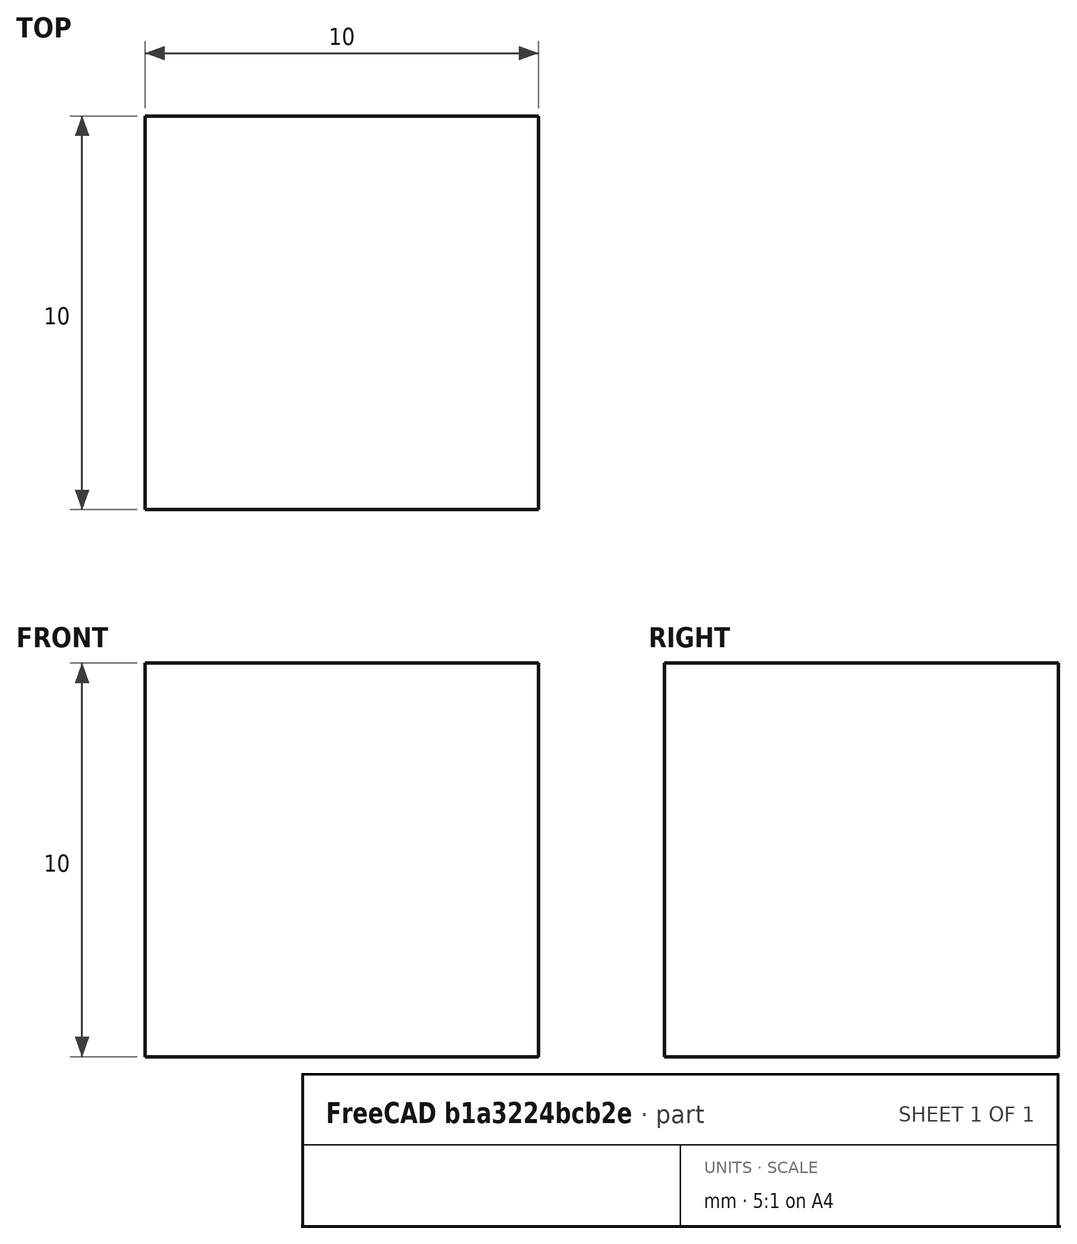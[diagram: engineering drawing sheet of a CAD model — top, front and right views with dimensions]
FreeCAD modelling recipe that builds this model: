
FCSTD DOCUMENT  (FreeCAD 0.21R33694 (Git))
Label: VM_Uniaxial_Tension_Example
License: All rights reserved
LicenseURL: http://en.wikipedia.org/wiki/All_rights_reserved
objects: Fem::ConstraintPressure×3, Fem::FemMeshObjectPython×2, Fem::ConstraintDisplacement×2, Part::Box×1, Fem::FemSolverObjectPython×1, App::MaterialObjectPython×1, Fem::ConstraintFixed×1, Fem::FemPostPipeline×1, Fem::FemResultObjectPython×1, Fem::FemAnalysis×1
note: 1 computed .brp shape members not serialized (recipe doc carries the construction recipe); baked Part::Feature solids carry a one-line shape summary decoded from their .brp

FEATURE [Part::Box] Box  label="Cube"
  AttacherType = Attacher::AttachEngine3D
  Height = 10
  Length = 10
  Width = 10
FEATURE [Fem::FemSolverObjectPython] SolverCcxTools  # FEM object (typed FeaturePython)
  AnalysisType = 0
  BeamShellResultOutput3D = false
  BucklingFactors = 1
  EigenmodeHighLimit = 1000000
  EigenmodeLowLimit = 0
  EigenmodesCount = 10
  GeometricalNonlinearity = 0
  IterationsControlParameterCutb = 0.25,0.5,0.75,0.85,,,1.5,
  IterationsControlParameterIter = 4,8,9,200,10,400,,200,,
  IterationsControlParameterTimeUse = false
  IterationsThermoMechMaximum = 2000
  IterationsUserDefinedIncrementations = false
  IterationsUserDefinedTimeStepLength = false
  MaterialNonlinearity = 0
  MatrixSolverType = 0
  SplitInputWriter = false
  ThermoMechSteadyState = true
  TimeEnd = 1
  TimeInitialStep = 0.01
FEATURE [Fem::FemMeshObjectPython] FEMMeshGmsh  # FEM object (typed FeaturePython)
  Algorithm2D = 0
  Algorithm3D = 0
  CharacteristicLengthMax = 10
  CharacteristicLengthMin = 10
  CoherenceMesh = true
  ElementDimension = 0
  ElementOrder = 1
  GeometryTolerance = 1e-06
  GroupsOfNodes = false
  HighOrderOptimize = 0
  MeshSizeFromCurvature = 12
  OptimizeNetgen = false
  OptimizeStd = true
  Part = -> Box
  RecombinationAlgorithm = 0
  Recombine3DAll = false
  RecombineAll = false
  SecondOrderLinear = false
FEATURE [Fem::ConstraintPressure] ConstraintPressure
  NormalDirection = (1,0,0)
  Normals = (18) [(1,0,0),(1,0,0),(1,0,0),(1,0,0),(1,0,0),(1,0,0),(1,0,0),(1,0,0),(1,0,0),(-1,0,0),(-1,0,0),(-1,0,0),(-1,0,0),(-1,0,0),(-1,0,0),(-1,0,0),(-1,0,0),+1 more]
  Points = (18) [(10,10,0),(10,10,5),(10,10,10),(10,5,0),(10,5,5),(10,5,10),(10,0,0),(10,0,5),(10,0,10),(0,10,0),(0,10,5),(0,10,10),(0,5,0),(0,5,5),(0,5,10),(0,0,0),+2 more]
  Pressure = 10
  References = -> [Box]
  Reversed = true
FEATURE [App::MaterialObjectPython] MaterialSolid  # material (typed FeaturePython)
  Category = 0
  Material = AuthorAndLicense=(c) 2013 Yorik van Havre (CC-BY 3.0),CardName=Concrete-Generic,CompressiveStrength=25 MPa,Density=2400 kg/m^3,+7 more (map truncated)
  References = -> [Box]
FEATURE [Fem::ConstraintPressure] ConstraintPressure001
  NormalDirection = (0,-1,0)
  Normals = (18) [(0,-1,0),(0,-1,0),(0,-1,0),(0,-1,0),(0,-1,0),(0,-1,0),(0,-1,0),(0,-1,0),(0,-1,0),(0,1,0),(0,1,0),(0,1,0),(0,1,0),(0,1,0),(0,1,0),(0,1,0),(0,1,0),+1 more]
  Points = (18) [(0,0,0),(0,0,5),(0,0,10),(5,0,0),(5,0,5),(5,0,10),(10,0,0),(10,0,5),(10,0,10),(0,10,0),(0,10,5),(0,10,10),(5,10,0),(5,10,5),(5,10,10),(10,10,0),+2 more]
  Pressure = 0
  References = -> [Box]
FEATURE [Fem::ConstraintPressure] ConstraintPressure002  label="ConstraintPressure002(p)"
  NormalDirection = (0,0,1)
  Normals = (18) [(0,0,1),(0,0,1),(0,0,1),(0,0,1),(0,0,1),(0,0,1),(0,0,1),(0,0,1),(0,0,1),(0,0,-1),(0,0,-1),(0,0,-1),(0,0,-1),(0,0,-1),(0,0,-1),(0,0,-1),(0,0,-1),+1 more]
  Points = (18) [(0,0,10),(5,0,10),(10,0,10),(0,5,10),(5,5,10),(10,5,10),(0,10,10),(5,10,10),(10,10,10),(0,0,0),(5,0,0),(10,0,0),(0,5,0),(5,5,0),(10,5,0),(0,10,0),+2 more]
  Pressure = 10
  References = -> [Box]
  Reversed = true
FEATURE [Fem::ConstraintFixed] ConstraintFixed
  NormalDirection = (0,0,1)
  Normals = (1) [(0,0,1)]
  Points = (1) [(0,0,0)]
  References = -> [Box]
  Scale = 2
FEATURE [Fem::ConstraintDisplacement] ConstraintDisplacement
  NormalDirection = (0,0,1)
  Normals = (2) [(0,0,1),(0,0,1)]
  Points = (2) [(0,10,0),(10,0,0)]
  References = -> [Box]
  Scale = 2
  hasXFormula = false
  hasYFormula = false
  hasZFormula = false
  rotxFix = false
  rotxFree = true
  rotyFix = false
  rotyFree = true
  rotzFix = false
  rotzFree = true
  useFlowSurfaceForce = false
  xDisplacement = 0
  xFix = false
  xFree = true
  xRotation = 0
  yDisplacement = 0
  yFix = false
  yFree = true
  yRotation = 0
  zDisplacement = 0
  zFix = false
  zFree = false
  zRotation = 0
FEATURE [Fem::ConstraintDisplacement] ConstraintDisplacement001
  NormalDirection = (0,0,1)
  Normals = (1) [(0,0,1)]
  Points = (1) [(0,10,0)]
  References = -> [Box]
  Scale = 2
  hasXFormula = false
  hasYFormula = false
  hasZFormula = false
  rotxFix = false
  rotxFree = true
  rotyFix = false
  rotyFree = true
  rotzFix = false
  rotzFree = true
  useFlowSurfaceForce = false
  xDisplacement = 0
  xFix = false
  xFree = false
  xRotation = 0
  yDisplacement = 0
  yFix = false
  yFree = true
  yRotation = 0
  zDisplacement = 0
  zFix = false
  zFree = true
  zRotation = 0
FEATURE [Fem::FemPostPipeline] Pipeline_CCX_Results
  Mode = 2
FEATURE [Fem::FemMeshObjectPython] Result_Mesh_Volume  # FEM object (typed FeaturePython)
FEATURE [Fem::FemResultObjectPython] ResultMechanical  # FEM object (typed FeaturePython)
  CriticalStrainRatio = [0,0,0,0,0,0,0,0,0,0,0,0,0,0,0,0,0,0,0,0,0,0,0,0,0,0,0,0,0,0,0,0,0,0,0,0,0,0,0,0,0,0,0,0,0,0,0,0,0,0,0,0,0,0,0,0,0,0,0,0,0,0,0]
  DisplacementLengths = [5.55312e-08,0,5.55312e-08,7.04761e-19,0.000643259,0.000643259,0.000643259,0.000643259,2.77656e-08,5.55312e-08,2.77656e-08,1.05319e-17,0.000643259,0.000643259,0.000643259,0.000643259,0.000321629,0.000321629,0.000321629,0.000321629,+43 more]
  DisplacementVectors = (63) [(3.73088e-17,8.64892e-18,-5.55312e-08),(0,0,0),(2.34631e-17,8.31972e-18,-5.55312e-08),(0,-7.04761e-19,0),(0.000643259,1.66696e-17,-5.55312e-08),+58 more]
  Eigenmode = 0
  EigenmodeFrequency = 0
  Mesh = -> Result_Mesh_Volume
  NodeNumbers = [1,2,3,4,5,6,7,8,9,10,11,12,13,14,15,16,17,18,19,20,21,22,23,24,25,26,27,28,29,30,31,32,33,34,35,36,37,38,39,40,41,42,43,44,45,46,47,48,49,50,51,52,53,54,55,56,57,58,59,60,61,62,63]
  NodeStressXX = [10,10,10,10,10,10,10,10,10,10,10,10,10,10,10,10,10,10,10,10,10,10,10,10,10,10,10,10,10,10,10,10,10,10,10,10,10,10,10,10,10,10,10,10,10,10,10,10,10,10,10,10,10,10,10,10,10,10,10,10,10,10,10]
  NodeStressXY = [2.31029e-15,1.52716e-14,-4.46962e-15,-3.1263e-15,-1.81075e-14,1.32062e-15,1.27714e-14,8.16305e-15,8.79093e-15,-1.07967e-15,-3.79796e-15,6.07264e-15,-8.39345e-15,-2.66807e-15,1.04672e-14,4.74184e-15,8.2961e-15,-7.89862e-15,2.51838e-15,+44 more]
  NodeStressXZ = [-2.12361e-15,7.94963e-15,8.80649e-17,4.58216e-15,1.10591e-15,-4.91706e-16,5.97468e-15,-4.20879e-15,2.91301e-15,-1.01777e-15,2.33511e-15,6.26589e-15,3.07103e-16,3.5403e-15,8.82943e-16,-2.35025e-15,3.72896e-15,-5.08848e-16,1.86682e-16,+44 more]
  NodeStressYY = [1.11022e-16,-2.16771e-14,-5.80438e-15,-6.39766e-15,-1.67227e-14,1.40166e-15,-1.37702e-14,-8.46719e-15,-1.0783e-14,-2.84668e-15,-6.10102e-15,-1.40374e-14,-7.66054e-15,-1.52465e-14,-1.11187e-14,-3.53276e-15,-1.01377e-14,-8.30586e-15,+45 more]
  NodeStressYZ = [1.47467e-15,7.25992e-15,3.40309e-16,4.53745e-16,-3.1195e-15,-2.24037e-15,-1.36123e-15,-4.53745e-15,4.36729e-15,9.0749e-16,3.97027e-16,3.85683e-15,-2.67993e-15,-2.24037e-15,-2.94934e-15,-3.38891e-15,2.50978e-15,-8.22413e-16,-2.04185e-15,+44 more]
  NodeStressZZ = [8.17394,8.17394,8.17394,8.17394,8.17394,8.17394,8.17394,8.17394,8.17394,8.17394,8.17394,8.17394,8.17394,8.17394,8.17394,8.17394,8.17394,8.17394,8.17394,8.17394,8.17394,8.17394,8.17394,8.17394,8.17394,8.17394,8.17394,8.17394,8.17394,8.17394,+33 more]
  Peeq = [0.00223275,0.00223275,0.00223275,0.00223275,0.00223275,0.00223275,0.00223275,0.00223275,0.00223275,0.00223275,0.00223275,0.00223275,0.00223275,0.00223275,0.00223275,0.00223275,0.00223275,0.00223275,0.00223275,0.00223275,0.00223275,+42 more]
  PrincipalMax = [0,-2.96888e-13,-9.93369e-14,-9.9777e-14,-6.77995e-13,0,-2.79028e-13,-2.11677e-13,-2.39413e-13,-3.01886e-14,-1.0296e-13,-1.62532e-13,-8.09059e-13,-1.56742e-13,-2.45353e-13,-1.16635e-13,-1.5924e-13,-1.70269e-13,-1.19927e-13,-1.44487e-13,+43 more]
  PrincipalMin = [81.7394,81.7394,81.7394,81.7394,81.7394,81.7394,81.7394,81.7394,81.7394,81.7394,81.7394,81.7394,81.7394,81.7394,81.7394,81.7394,81.7394,81.7394,81.7394,81.7394,81.7394,81.7394,81.7394,81.7394,81.7394,81.7394,81.7394,81.7394,81.7394,81.7394,+33 more]
  ResultType = Fem::ResultMechanical
  Stats = [0,0.000643259,-7.04761e-19,1.69501e-17,-5.55312e-08,2.33683e-19,0,0.000643259,100,100,-8.09059e-13,2.70551e-14,0,0,81.7394,81.7394,0,0,0.00223275,0.00223275,0,0,0,0,0,0]
  Temperature = [0,0,0,0,0,0,0,0,0,0,0,0,0,0,0,0,0,0,0,0,0,0,0,0,0,0,0,0,0,0,0,0,0,0,0,0,0,0,0,0,0,0,0,0,0,0,0,0,0,0,0,0,0,0,0,0,0,0,0,0,0,0,0]
  Time = 0
  vonMises = [100,100,100,100,100,100,100,100,100,100,100,100,100,100,100,100,100,100,100,100,100,100,100,100,100,100,100,100,100,100,100,100,100,100,100,100,100,100,100,100,100,100,100,100,100,100,100,100,100,100,100,100,100,100,100,100,100,100,100,100,+3 more]
FEATURE [Fem::FemAnalysis] Analysis
  Group = -> [SolverCcxTools,FEMMeshGmsh,ConstraintPressure,MaterialSolid,ConstraintPressure001,ConstraintPressure002,ConstraintFixed,ConstraintDisplacement,ConstraintDisplacement001,Pipeline_CCX_Results,ResultMechanical]
